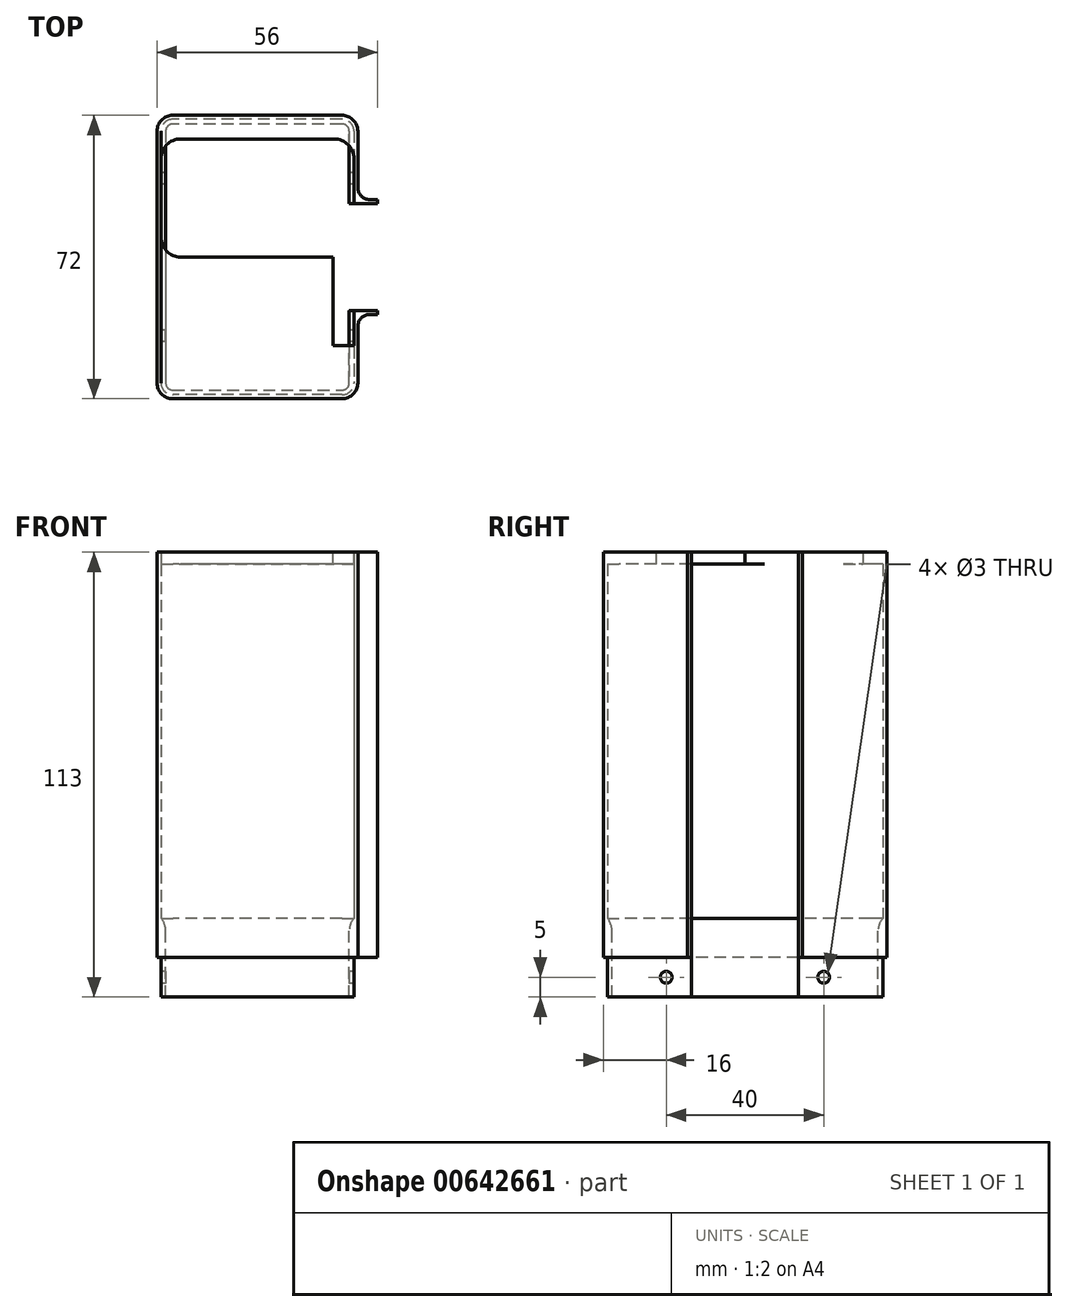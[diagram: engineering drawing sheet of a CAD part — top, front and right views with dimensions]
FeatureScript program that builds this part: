
annotation { "Feature Type Name" : "Feature", "Feature Type Description" : "" }
export const myFeature = defineFeature(function(context is Context, id is Id, definition is map)
    precondition{}
    {
        {
            var Q0;
            Q0=qCreatedBy(makeId("Top.planeOp"),FACE);
            var sketch = newSketch(context, id + "F0", { "sketchPlane" : qUnion([Q0])});
            skLineSegment(sketch, "E0.bottom", {"start": v(21.5, 35) * mm, "end": v(-21.5, 35) * mm});
            skLineSegment(sketch, "E0.top", {"start": v(21.5, -35) * mm, "end": v(-21.5, -35) * mm});
            skLineSegment(sketch, "E0.left", {"start": v(24.5, 32) * mm, "end": v(24.5, 13.63) * mm});
            skLineSegment(sketch, "E0.right", {"start": v(-24.5, 32) * mm, "end": v(-24.5, -32) * mm});
            skPoint(sketch, "E0.middle", {"position": v(0, 0) * mm});
            skPoint(sketch, "E1", {"position": v(24.5, 13.63) * mm});
            skPoint(sketch, "E2", {"position": v(24.5, -13.62) * mm});
            skLineSegment(sketch, "E3.trimOffspring", {"start": v(24.5, -13.62) * mm, "end": v(24.5, -32) * mm});
            skPoint(sketch, "E4.visualSharp", {"position": v(24.5, 35) * mm});
            skArc(sketch, "E4.filletArc", {"start": v(24.5, 32) * mm, "mid": v(23.62, 34.12) * mm, "end": v(21.5, 35) * mm});
            skPoint(sketch, "E5.visualSharp", {"position": v(-24.5, 35) * mm});
            skArc(sketch, "E5.filletArc", {"start": v(-21.5, 35) * mm, "mid": v(-23.62, 34.12) * mm, "end": v(-24.5, 32) * mm});
            skPoint(sketch, "E6.visualSharp", {"position": v(-24.5, -35) * mm});
            skArc(sketch, "E6.filletArc", {"start": v(-24.5, -32) * mm, "mid": v(-23.62, -34.12) * mm, "end": v(-21.5, -35) * mm});
            skPoint(sketch, "E7.visualSharp", {"position": v(24.5, -35) * mm});
            skArc(sketch, "E7.filletArc", {"start": v(21.5, -35) * mm, "mid": v(23.62, -34.12) * mm, "end": v(24.5, -32) * mm});
            skLineSegment(sketch, "E8", {"start": v(24.5, 13.63) * mm, "end": v(30.5, 13.63) * mm});
            skLineSegment(sketch, "E9", {"start": v(24.5, -13.62) * mm, "end": v(30.5, -13.62) * mm});
            skLineSegment(sketch, "E10.0", {"start": v(28.5, -14.62) * mm, "end": v(30.5, -14.62) * mm});
            skLineSegment(sketch, "E10.1", {"start": v(21.5, 36) * mm, "end": v(-21.5, 36) * mm});
            skArc(sketch, "E10.2", {"start": v(25.5, 32) * mm, "mid": v(24.33, 34.83) * mm, "end": v(21.5, 36) * mm});
            skLineSegment(sketch, "E10.3", {"start": v(25.5, 32) * mm, "end": v(25.5, 17.63) * mm});
            skLineSegment(sketch, "E10.4", {"start": v(28.5, 14.63) * mm, "end": v(30.5, 14.63) * mm});
            skArc(sketch, "E10.5", {"start": v(-21.5, 36) * mm, "mid": v(-24.33, 34.83) * mm, "end": v(-25.5, 32) * mm});
            skLineSegment(sketch, "E10.6", {"start": v(-25.5, 32) * mm, "end": v(-25.5, -32) * mm});
            skArc(sketch, "E10.7", {"start": v(-25.5, -32) * mm, "mid": v(-24.33, -34.83) * mm, "end": v(-21.5, -36) * mm});
            skLineSegment(sketch, "E10.8", {"start": v(21.5, -36) * mm, "end": v(-21.5, -36) * mm});
            skArc(sketch, "E10.9", {"start": v(21.5, -36) * mm, "mid": v(24.33, -34.83) * mm, "end": v(25.5, -32) * mm});
            skLineSegment(sketch, "E10.10", {"start": v(25.5, -17.62) * mm, "end": v(25.5, -32) * mm});
            skLineSegment(sketch, "E11", {"start": v(30.5, -13.62) * mm, "end": v(30.5, -14.62) * mm});
            skLineSegment(sketch, "E12", {"start": v(30.5, 14.63) * mm, "end": v(30.5, 13.63) * mm});
            skPoint(sketch, "E13.visualSharp", {"position": v(25.5, -14.62) * mm});
            skArc(sketch, "E13.filletArc", {"start": v(28.5, -14.62) * mm, "mid": v(26.38, -15.5) * mm, "end": v(25.5, -17.62) * mm});
            skPoint(sketch, "E14.visualSharp", {"position": v(25.5, 14.63) * mm});
            skArc(sketch, "E14.filletArc", {"start": v(25.5, 17.63) * mm, "mid": v(26.38, 15.5) * mm, "end": v(28.5, 14.63) * mm});
            skSolve(sketch);
        }
        {
            var Q0;
            Q0=qSketchRegion(id+"F0",true);
            extrude(context, id + "F1", {"entities" : qUnion([Q0]), "depth" : 100 * mm, "offsetDistance" : 25 * mm});
        }
        {
            var Q0;
            Q0=makeQuery(id+"F1.opExtrude","CAP_FACE",FACE,{"disambiguationData":[OSD([sQuery(id+"F0.wireOp",EDGE,"E0.bottom"),sQuery(id+"F0.wireOp",EDGE,"E0.top"),sQuery(id+"F0.wireOp",EDGE,"E0.left"),sQuery(id+"F0.wireOp",EDGE,"E0.right"),sQuery(id+"F0.wireOp",EDGE,"E3.trimOffspring"),sQuery(id+"F0.wireOp",EDGE,"E4.filletArc"),sQuery(id+"F0.wireOp",EDGE,"E5.filletArc"),sQuery(id+"F0.wireOp",EDGE,"E6.filletArc"),sQuery(id+"F0.wireOp",EDGE,"E7.filletArc"),sQuery(id+"F0.wireOp",EDGE,"E8"),sQuery(id+"F0.wireOp",EDGE,"E9"),sQuery(id+"F0.wireOp",EDGE,"E10.0"),sQuery(id+"F0.wireOp",EDGE,"E10.1"),sQuery(id+"F0.wireOp",EDGE,"E10.2"),sQuery(id+"F0.wireOp",EDGE,"E10.3"),sQuery(id+"F0.wireOp",EDGE,"E10.4"),sQuery(id+"F0.wireOp",EDGE,"E10.5"),sQuery(id+"F0.wireOp",EDGE,"E10.6"),sQuery(id+"F0.wireOp",EDGE,"E10.7"),sQuery(id+"F0.wireOp",EDGE,"E10.8"),sQuery(id+"F0.wireOp",EDGE,"E10.9"),sQuery(id+"F0.wireOp",EDGE,"E10.10"),sQuery(id+"F0.wireOp",EDGE,"E11"),sQuery(id+"F0.wireOp",EDGE,"E12"),sQuery(id+"F0.wireOp",EDGE,"E13.filletArc"),sQuery(id+"F0.wireOp",EDGE,"E14.filletArc")])],"isStart":false});
            var sketch = newSketch(context, id + "F2", { "sketchPlane" : qUnion([Q0])});
            skLineSegment(sketch, "E15", {"start": v(24.5, -13.62) * mm, "end": v(24.5, 0) * mm});
            skLineSegment(sketch, "E16", {"start": v(24.5, 0) * mm, "end": v(-24.5, 0) * mm});
            skLineSegment(sketch, "E17", {"start": v(-24.5, 30) * mm, "end": v(24.5, 30) * mm});
            skSolve(sketch);
        }
        {
            var Q0;
            Q0=makeQuery(id+"F2.imprint","IMPRINT",FACE,{"disambiguationData":[TD([[makeQuery(id+"F2.imprint","IMPRINT",EDGE,{"derivedFrom":sQuery(id+"F2.wireOp",EDGE,"E15")}),1.0]])]});
            var Q1;
            Q1=makeQuery(id+"F2.imprint","IMPRINT",FACE,{"disambiguationData":[TD([[makeQuery(id+"F2.imprint","IMPRINT",EDGE,{"derivedFrom":makeQuery(id+"F1.opExtrude","CAP_EDGE",EDGE,{"disambiguationData":[OSD([sQuery(id+"F0.wireOp",EDGE,"E0.bottom")])],"isStart":false})}),-1.0]])]});
            var Q2;
            {var subQ2=sQuery(id+"F2.wireOp",EDGE,"E17");Q2=makeQuery(id+"F2.imprint","IMPRINT",FACE,{"disambiguationData":[TD([[makeQuery(id+"F2.imprint","IMPRINT",EDGE,{"derivedFrom":subQ2}),1.0]])]});}
            extrude(context, id + "F3", {"entities" : qUnion([Q0, Q1, Q2]), "operationType" : NewBodyOperationType.ADD, "depth" : 3 * mm, "offsetDistance" : 25 * mm});
        }
        {
            var Q0;
            Q0=makeQuery(id+"F1.opExtrude","CAP_FACE",FACE,{"disambiguationData":[OSD([sQuery(id+"F0.wireOp",EDGE,"E0.bottom"),sQuery(id+"F0.wireOp",EDGE,"E0.top"),sQuery(id+"F0.wireOp",EDGE,"E0.left"),sQuery(id+"F0.wireOp",EDGE,"E0.right"),sQuery(id+"F0.wireOp",EDGE,"E3.trimOffspring"),sQuery(id+"F0.wireOp",EDGE,"E4.filletArc"),sQuery(id+"F0.wireOp",EDGE,"E5.filletArc"),sQuery(id+"F0.wireOp",EDGE,"E6.filletArc"),sQuery(id+"F0.wireOp",EDGE,"E7.filletArc"),sQuery(id+"F0.wireOp",EDGE,"E8"),sQuery(id+"F0.wireOp",EDGE,"E9"),sQuery(id+"F0.wireOp",EDGE,"E10.0"),sQuery(id+"F0.wireOp",EDGE,"E10.1"),sQuery(id+"F0.wireOp",EDGE,"E10.2"),sQuery(id+"F0.wireOp",EDGE,"E10.3"),sQuery(id+"F0.wireOp",EDGE,"E10.4"),sQuery(id+"F0.wireOp",EDGE,"E10.5"),sQuery(id+"F0.wireOp",EDGE,"E10.6"),sQuery(id+"F0.wireOp",EDGE,"E10.7"),sQuery(id+"F0.wireOp",EDGE,"E10.8"),sQuery(id+"F0.wireOp",EDGE,"E10.9"),sQuery(id+"F0.wireOp",EDGE,"E10.10"),sQuery(id+"F0.wireOp",EDGE,"E11"),sQuery(id+"F0.wireOp",EDGE,"E12"),sQuery(id+"F0.wireOp",EDGE,"E13.filletArc"),sQuery(id+"F0.wireOp",EDGE,"E14.filletArc")])],"isStart":true});
            var sketch = newSketch(context, id + "F4", { "sketchPlane" : qUnion([Q0])});
            skLineSegment(sketch, "E18.0", {"start": v(23.3, -32) * mm, "end": v(23.3, -13.63) * mm});
            skArc(sketch, "E18.1", {"start": v(23.3, -32) * mm, "mid": v(22.77, -33.27) * mm, "end": v(21.5, -33.8) * mm});
            skLineSegment(sketch, "E18.2", {"start": v(21.5, -33.8) * mm, "end": v(-21.5, -33.8) * mm});
            skArc(sketch, "E18.3", {"start": v(-21.5, -33.8) * mm, "mid": v(-22.77, -33.27) * mm, "end": v(-23.3, -32) * mm});
            skLineSegment(sketch, "E18.4", {"start": v(-23.3, -32) * mm, "end": v(-23.3, 32) * mm});
            skLineSegment(sketch, "E18.5", {"start": v(23.3, 13.62) * mm, "end": v(23.3, 32) * mm});
            skArc(sketch, "E18.6", {"start": v(21.5, 33.8) * mm, "mid": v(22.77, 33.27) * mm, "end": v(23.3, 32) * mm});
            skLineSegment(sketch, "E18.7", {"start": v(21.5, 33.8) * mm, "end": v(-21.5, 33.8) * mm});
            skArc(sketch, "E18.8", {"start": v(-23.3, 32) * mm, "mid": v(-22.77, 33.27) * mm, "end": v(-21.5, 33.8) * mm});
            skLineSegment(sketch, "E19", {"start": v(24.5, 13.62) * mm, "end": v(23.3, 13.62) * mm});
            skLineSegment(sketch, "E20", {"start": v(23.3, -13.63) * mm, "end": v(24.5, -13.63) * mm});
            skSolve(sketch);
        }
        {
            var Q0;
            Q0=makeQuery(id+"F4.imprint","IMPRINT",FACE,{"disambiguationData":[TD([[makeQuery(id+"F4.imprint","IMPRINT",EDGE,{"derivedFrom":sQuery(id+"F4.wireOp",EDGE,"E18.0")}),-1.0]])]});
            extrude(context, id + "F5", {"entities" : qUnion([Q0]), "operationType" : NewBodyOperationType.ADD, "endBound" : BoundingType.SYMMETRIC, "depth" : 20 * mm, "offsetDistance" : 25 * mm});
        }
        {
            var Q0;
            Q0=makeQuery(id+"F5.opExtrude","SWEPT_FACE",FACE,{"disambiguationData":[OSD([sQuery(id+"F0.wireOp",EDGE,"E0.right")])]});
            var sketch = newSketch(context, id + "F6", { "sketchPlane" : qUnion([Q0])});
            skCircle(sketch, "E21", {"center": v(-20, -5) * mm, "radius": 1.5 * mm});
            skCircle(sketch, "E22", {"center": v(20, -5) * mm, "radius": 1.5 * mm});
            skLineSegment(sketch, "E23", {"start": v(-20, -5) * mm, "end": v(20, -5) * mm, "construction": true});
            skPoint(sketch, "E24", {"position": v(0, -5) * mm});
            skLineSegment(sketch, "E25", {"start": v(0, 0) * mm, "end": v(0, -10) * mm, "construction": true});
            skSolve(sketch);
        }
        {
            var Q0;
            Q0=qSketchRegion(id+"F6",true);
            extrude(context, id + "F7", {"entities" : qUnion([Q0]), "operationType" : NewBodyOperationType.REMOVE, "endBound" : BoundingType.THROUGH_ALL, "oppositeDirection" : true, "depth" : 25 * mm, "offsetDistance" : 25 * mm});
        }
        {
            var Q0;
            {var subQ0=sQuery(id+"F4.wireOp",EDGE,"E18.0");Q0=makeQuery(id+"F5.boolean.opBoolean","SPLIT",EDGE,{"disambiguationData":[topologyDisambiguationEdgeConnected([makeQuery(id+"F5.opExtrude","CAP_FACE",FACE,{"disambiguationData":[OSD([sQuery(id+"F0.wireOp",EDGE,"E0.bottom"),sQuery(id+"F0.wireOp",EDGE,"E0.top"),sQuery(id+"F0.wireOp",EDGE,"E0.left"),sQuery(id+"F0.wireOp",EDGE,"E0.right"),sQuery(id+"F0.wireOp",EDGE,"E3.trimOffspring"),sQuery(id+"F0.wireOp",EDGE,"E4.filletArc"),sQuery(id+"F0.wireOp",EDGE,"E5.filletArc"),sQuery(id+"F0.wireOp",EDGE,"E6.filletArc"),sQuery(id+"F0.wireOp",EDGE,"E7.filletArc"),subQ0,sQuery(id+"F4.wireOp",EDGE,"E18.1"),sQuery(id+"F4.wireOp",EDGE,"E18.2"),sQuery(id+"F4.wireOp",EDGE,"E18.3"),sQuery(id+"F4.wireOp",EDGE,"E18.4"),sQuery(id+"F4.wireOp",EDGE,"E18.5"),sQuery(id+"F4.wireOp",EDGE,"E18.6"),sQuery(id+"F4.wireOp",EDGE,"E18.7"),sQuery(id+"F4.wireOp",EDGE,"E18.8"),sQuery(id+"F4.wireOp",EDGE,"E19"),sQuery(id+"F4.wireOp",EDGE,"E20")])],"isStart":true})])],"derivedFrom":makeQuery(id+"F5.opExtrude","CAP_EDGE",EDGE,{"disambiguationData":[OSD([subQ0])],"isStart":true})});}
            fillet(context, id + "F8", {"entities" : qUnion([Q0]), "radius" : 5 * mm, "tangentPropagation" : true, "allowEdgeOverflow" : false});
        }
        {
            var Q0;
            Q0=makeQuery(id+"F3.opExtrude","CAP_FACE",FACE,{"disambiguationData":[OSD([sQuery(id+"F0.wireOp",EDGE,"E0.left"),sQuery(id+"F0.wireOp",EDGE,"E0.right"),sQuery(id+"F0.wireOp",EDGE,"E8"),sQuery(id+"F0.wireOp",EDGE,"E9"),sQuery(id+"F0.wireOp",EDGE,"E10.0"),sQuery(id+"F0.wireOp",EDGE,"E10.1"),sQuery(id+"F0.wireOp",EDGE,"E10.2"),sQuery(id+"F0.wireOp",EDGE,"E10.3"),sQuery(id+"F0.wireOp",EDGE,"E10.4"),sQuery(id+"F0.wireOp",EDGE,"E10.5"),sQuery(id+"F0.wireOp",EDGE,"E10.6"),sQuery(id+"F0.wireOp",EDGE,"E10.7"),sQuery(id+"F0.wireOp",EDGE,"E10.8"),sQuery(id+"F0.wireOp",EDGE,"E10.9"),sQuery(id+"F0.wireOp",EDGE,"E10.10"),sQuery(id+"F0.wireOp",EDGE,"E11"),sQuery(id+"F0.wireOp",EDGE,"E12"),sQuery(id+"F0.wireOp",EDGE,"E13.filletArc"),sQuery(id+"F0.wireOp",EDGE,"E14.filletArc"),sQuery(id+"F2.wireOp",EDGE,"E15"),sQuery(id+"F2.wireOp",EDGE,"E16"),sQuery(id+"F2.wireOp",EDGE,"E17")])],"isStart":false});
            var sketch = newSketch(context, id + "F9", { "sketchPlane" : qUnion([Q0])});
            skLineSegment(sketch, "E26.bottom", {"start": v(24.5, 0) * mm, "end": v(19.23, 0) * mm});
            skLineSegment(sketch, "E26.top", {"start": v(24.5, -22.44) * mm, "end": v(19.23, -22.44) * mm});
            skLineSegment(sketch, "E26.left", {"start": v(24.5, 0) * mm, "end": v(24.5, -22.44) * mm});
            skLineSegment(sketch, "E26.right", {"start": v(19.23, 0) * mm, "end": v(19.23, -22.44) * mm});
            skSolve(sketch);
        }
        {
            var Q0;
            Q0 = qSketchRegion(id + "F9", true);
            extrude(context, id + "F10", {"entities" : qUnion([Q0]), "operationType" : NewBodyOperationType.REMOVE, "oppositeDirection" : true, "depth" : 25 * mm, "offsetDistance" : 25 * mm});
        }
        {
            var Q0;
            {var subQ3=sQuery(id+"F9.wireOp",EDGE,"E26.bottom");Q0=makeQuery(id+"F9.imprint","IMPRINT",FACE,{"disambiguationData":[TD([[makeQuery(id+"F9.imprint","IMPRINT",EDGE,{"derivedFrom":subQ3}),1.0]])]});}
            extrude(context, id + "F11", {"entities" : qUnion([Q0]), "operationType" : NewBodyOperationType.REMOVE, "oppositeDirection" : true, "depth" : 22.3 * mm, "offsetDistance" : 25 * mm});
        }
        {
            var Q0;
            Q0=makeQuery(id+"F3.opExtrude","SWEPT_EDGE",EDGE,{"disambiguationData":[OSD([sQuery(id+"F0.wireOp",EDGE,"E0.right"),sQuery(id+"F2.wireOp",EDGE,"E16")])]});
            var Q1;
            Q1=makeQuery(id+"F3.opExtrude","SWEPT_EDGE",EDGE,{"disambiguationData":[OSD([sQuery(id+"F2.wireOp",EDGE,"E15"),sQuery(id+"F2.wireOp",EDGE,"E16")])]});
            var Q2;
            Q2=makeQuery(id+"F10.boolean.opBoolean","COPY",EDGE,{"derivedFrom":makeQuery(id+"F10.opExtrude","SWEPT_EDGE",EDGE,{"disambiguationData":[OSD([sQuery(id+"F2.wireOp",EDGE,"E16"),sQuery(id+"F9.wireOp",EDGE,"E26.bottom"),sQuery(id+"F9.wireOp",EDGE,"E26.right")])]})});
            fillet(context, id + "F12", {"entities" : qUnion([Q0, Q1, Q2]), "radius" : 5 * mm, "tangentPropagation" : true, "allowEdgeOverflow" : false});
        }
        {
            var Q0;
            Q0=makeQuery(id+"F3.opExtrude","SWEPT_EDGE",EDGE,{"disambiguationData":[OSD([sQuery(id+"F0.wireOp",EDGE,"E0.right"),sQuery(id+"F2.wireOp",EDGE,"E17")])]});
            var Q1;
            Q1=makeQuery(id+"F3.opExtrude","SWEPT_EDGE",EDGE,{"disambiguationData":[OSD([sQuery(id+"F0.wireOp",EDGE,"E0.left"),sQuery(id+"F2.wireOp",EDGE,"E17")])]});
            fillet(context, id + "F13", {"entities" : qUnion([Q0, Q1]), "radius" : 5 * mm, "tangentPropagation" : true, "allowEdgeOverflow" : false});
        }
    });
